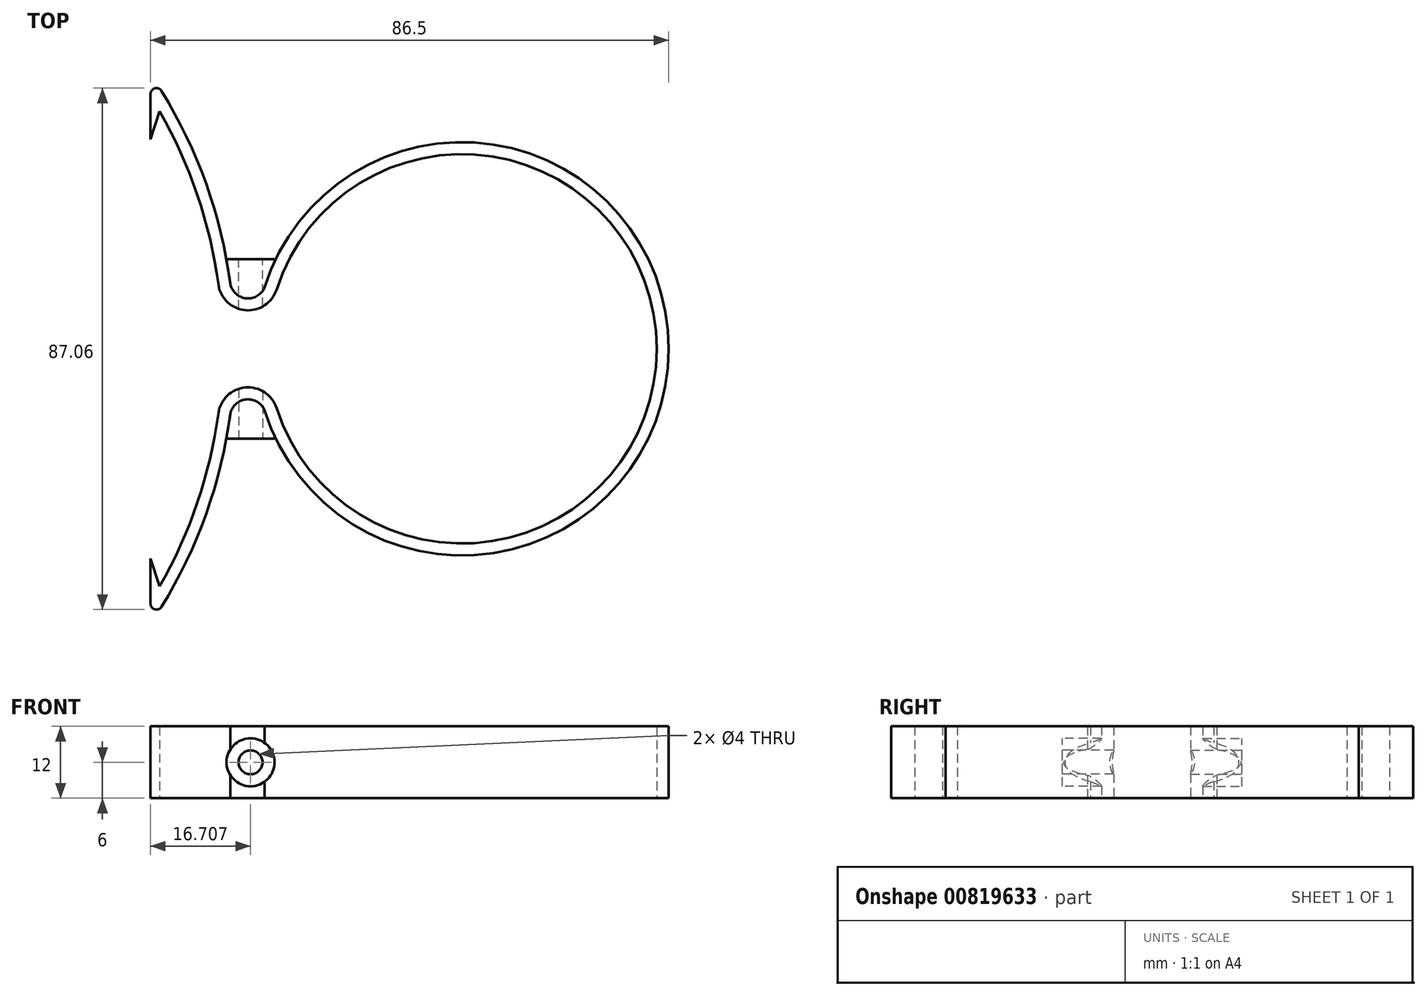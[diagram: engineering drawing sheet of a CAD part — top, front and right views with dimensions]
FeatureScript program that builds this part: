
annotation { "Feature Type Name" : "Feature", "Feature Type Description" : "" }
export const myFeature = defineFeature(function(context is Context, id is Id, definition is map)
    precondition{}
    {
        {
            var Q0;
            Q0=qCreatedBy(makeId("Top.planeOp"),FACE);
            var sketch = newSketch(context, id + "F0", { "sketchPlane" : qUnion([Q0])});
            skArc(sketch, "E0", {"start": v(-31.22, -9.04) * mm, "mid": v(32.5, 0) * mm, "end": v(-31.22, 9.04) * mm});
            skLineSegment(sketch, "E1", {"start": v(0, 0) * mm, "end": v(-50, 0) * mm, "construction": true});
            skLineSegment(sketch, "E2", {"start": v(-50, 0) * mm, "end": v(-50, 41) * mm, "construction": true});
            skLineSegment(sketch, "E3", {"start": v(-50, 35) * mm, "end": v(-48, 35) * mm, "construction": true});
            skLineSegment(sketch, "E4.MirrorCS", {"start": v(-52, 35) * mm, "end": v(-50.45, 39.65) * mm});
            skLineSegment(sketch, "E5.MirrorCS", {"start": v(-50, 35) * mm, "end": v(-52, 35) * mm, "construction": true});
            skArc(sketch, "E6.0", {"start": v(-32.93, -10.29) * mm, "mid": v(34.5, 0) * mm, "end": v(-32.93, 10.29) * mm});
            skLineSegment(sketch, "E7", {"start": v(-52, 35) * mm, "end": v(-52, 45.93) * mm});
            skArc(sketch, "E8", {"start": v(-40.67, 10.76) * mm, "mid": v(-44.17, 25.67) * mm, "end": v(-50.45, 39.65) * mm});
            skArc(sketch, "E9.0", {"start": v(-38.66, 10.79) * mm, "mid": v(-43.29, 29.13) * mm, "end": v(-52, 45.93) * mm});
            skPoint(sketch, "E10.orphan", {"position": v(-50, 41) * mm});
            skArc(sketch, "E11", {"start": v(-40.67, 10.76) * mm, "mid": v(-36.15, 6.45) * mm, "end": v(-30.95, 9.9) * mm});
            skArc(sketch, "E12", {"start": v(-38.72, 11.27) * mm, "mid": v(-35.98, 8.43) * mm, "end": v(-32.78, 10.74) * mm});
            skLineSegment(sketch, "E13.MirrorCS", {"start": v(-52, -35) * mm, "end": v(-52, -45.93) * mm});
            skArc(sketch, "E14.MirrorCS", {"start": v(-38.66, -10.79) * mm, "mid": v(-43.29, -29.13) * mm, "end": v(-52, -45.93) * mm});
            skArc(sketch, "E15.MirrorCS", {"start": v(-40.67, -10.76) * mm, "mid": v(-44.17, -25.67) * mm, "end": v(-50.45, -39.65) * mm});
            skArc(sketch, "E16.MirrorCS", {"start": v(-40.67, -10.76) * mm, "mid": v(-36.15, -6.45) * mm, "end": v(-30.95, -9.9) * mm});
            skArc(sketch, "E17.MirrorCS", {"start": v(-38.72, -11.27) * mm, "mid": v(-35.98, -8.43) * mm, "end": v(-32.78, -10.74) * mm});
            skLineSegment(sketch, "E18.MirrorCS", {"start": v(-52, -35) * mm, "end": v(-50.45, -39.65) * mm});
            skSolve(sketch);
        }
        {
            var Q0;
            Q0 = qSketchRegion(id + "F0", true);
            extrude(context, id + "F1", {"entities" : qUnion([Q0]), "depth" : 12 * mm, "offsetDistance" : 25 * mm});
        }
        {
            var Q0;
            Q0=qCreatedBy(makeId("Front.planeOp"),FACE);
            cPlane(context, id + "F2", {"entities" : qUnion([Q0]), "cplaneType" : CPlaneType.OFFSET, "offset" : 15 * mm, "width" : 150 * mm, "height" : 150 * mm});
        }
        {
            var Q0;
            Q0=qCreatedBy(id+"F2.planeOp",FACE);
            var sketch = newSketch(context, id + "F3", { "sketchPlane" : qUnion([Q0])});
            skLineSegment(sketch, "E19.0.0", {"start": v(-38.66, 0) * mm, "end": v(-32.93, 0) * mm, "construction": true});
            skLineSegment(sketch, "E19.0.1", {"start": v(-32.93, 0) * mm, "end": v(-32.93, 12) * mm, "construction": true});
            skLineSegment(sketch, "E19.0.2", {"start": v(-32.93, 12) * mm, "end": v(-38.66, 12) * mm, "construction": true});
            skLineSegment(sketch, "E19.0.3", {"start": v(-38.66, 12) * mm, "end": v(-38.66, 0) * mm, "construction": true});
            skLineSegment(sketch, "E20", {"start": v(-32.93, 12) * mm, "end": v(-38.66, 0) * mm, "construction": true});
            skLineSegment(sketch, "E21", {"start": v(-38.66, 12) * mm, "end": v(-32.93, 0) * mm, "construction": true});
            skCircle(sketch, "E22", {"center": v(-35.3, 6) * mm, "radius": 4 * mm});
            skPoint(sketch, "E22.centerSnap0", {"position": v(-35.8, 6) * mm});
            skCircle(sketch, "E23", {"center": v(-35.3, 6) * mm, "radius": 2 * mm});
            skSolve(sketch);
        }
        {
            var Q0;
            Q0=makeQuery(id+"F3.imprint","IMPRINT",FACE,{"disambiguationData":[TD([[makeQuery(id+"F3.imprint","IMPRINT",EDGE,{"derivedFrom":sQuery(id+"F3.wireOp",EDGE,"E22")}),1.0]])]});
            var Q1;
            Q1=makeQuery(id+"F1.opExtrude","SWEPT_BODY",BODY,{"disambiguationData":[OSD([sQuery(id+"F0.wireOp",EDGE,"E0"),sQuery(id+"F0.wireOp",EDGE,"E4.MirrorCS"),sQuery(id+"F0.wireOp",EDGE,"E6.0"),sQuery(id+"F0.wireOp",EDGE,"E7"),sQuery(id+"F0.wireOp",EDGE,"E8"),sQuery(id+"F0.wireOp",EDGE,"E9.0"),sQuery(id+"F0.wireOp",EDGE,"E11"),sQuery(id+"F0.wireOp",EDGE,"E12"),sQuery(id+"F0.wireOp",EDGE,"E13.MirrorCS"),sQuery(id+"F0.wireOp",EDGE,"E14.MirrorCS"),sQuery(id+"F0.wireOp",EDGE,"E15.MirrorCS"),sQuery(id+"F0.wireOp",EDGE,"E16.MirrorCS"),sQuery(id+"F0.wireOp",EDGE,"E17.MirrorCS"),sQuery(id+"F0.wireOp",EDGE,"E18.MirrorCS")])]});
            extrude(context, id + "F4", {"entities" : qUnion([Q0]), "endBound" : BoundingType.UP_TO_BODY, "oppositeDirection" : true, "depth" : 15 * mm, "endBoundEntityBody" : qUnion([Q1]), "offsetDistance" : 25 * mm});
        }
        {
            var Q0;
            Q0=makeQuery(id+"F4.opExtrude","SWEPT_BODY",BODY,{"disambiguationData":[OSD([sQuery(id+"F3.wireOp",EDGE,"E22")])]});
            var Q1;
            Q1=qCreatedBy(makeId("Front.planeOp"),FACE);
            mirror(context, id + "F5", {"operationType" : NewBodyOperationType.ADD, "entities" : qUnion([Q0]), "mirrorPlane" : qUnion([Q1])});
        }
        {
            var Q0;
            Q0=makeQuery(id+"F3.imprint","IMPRINT",FACE,{"disambiguationData":[TD([[makeQuery(id+"F3.imprint","IMPRINT",EDGE,{"derivedFrom":sQuery(id+"F3.wireOp",EDGE,"E23")}),1.0]])]});
            extrude(context, id + "F6", {"entities" : qUnion([Q0]), "operationType" : NewBodyOperationType.REMOVE, "oppositeDirection" : true, "depth" : 100 * mm, "offsetDistance" : 25 * mm});
        }
        {
            var Q0;
            Q0=makeQuery(id+"F1.opExtrude","SWEPT_EDGE",EDGE,{"disambiguationData":[OSD([sQuery(id+"F0.wireOp",EDGE,"E13.MirrorCS"),sQuery(id+"F0.wireOp",EDGE,"E14.MirrorCS")])]});
            var Q1;
            Q1=makeQuery(id+"F1.opExtrude","SWEPT_EDGE",EDGE,{"disambiguationData":[OSD([sQuery(id+"F0.wireOp",EDGE,"E7"),sQuery(id+"F0.wireOp",EDGE,"E9.0")])]});
            fillet(context, id + "F7", {"entities" : qUnion([Q0, Q1]), "radius" : 1 * mm, "tangentPropagation" : true, "allowEdgeOverflow" : false});
        }
    });
